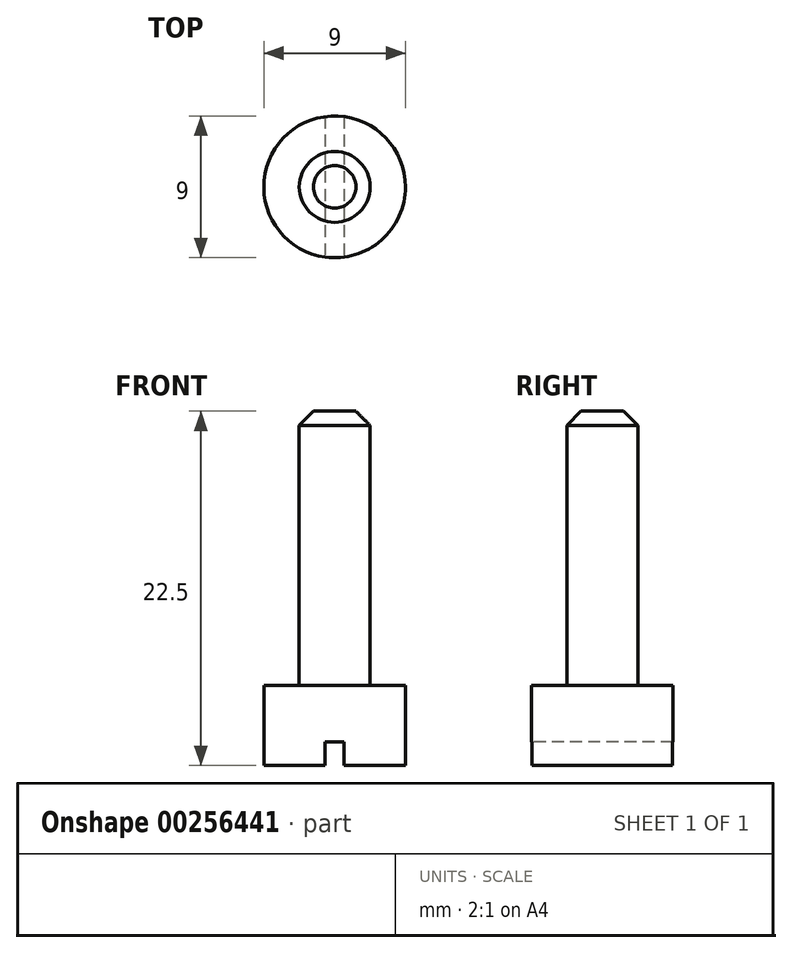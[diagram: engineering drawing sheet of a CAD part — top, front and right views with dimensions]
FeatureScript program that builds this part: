
annotation { "Feature Type Name" : "Feature", "Feature Type Description" : "" }
export const myFeature = defineFeature(function(context is Context, id is Id, definition is map)
    precondition{}
    {
        {
            var Q0;
            Q0=qCreatedBy(makeId("Top.planeOp"),FACE);
            var sketch = newSketch(context, id + "F0", { "sketchPlane" : qUnion([Q0])});
            skArc(sketch, "E0", {"start": v(-0.2, 1.49) * mm, "mid": v(-1.5, 0) * mm, "end": v(-0.2, -1.49) * mm});
            skLineSegment(sketch, "E1", {"start": v(-0.2, 1.49) * mm, "end": v(-0.2, -1.49) * mm});
            skLineSegment(sketch, "E2", {"start": v(0.2, 1.49) * mm, "end": v(0.2, -1.49) * mm});
            skArc(sketch, "E3.trimOffspring", {"start": v(0.2, -1.49) * mm, "mid": v(1.5, 0) * mm, "end": v(0.2, 1.49) * mm});
            skSolve(sketch);
        }
        {
            var Q0;
            {Q0=qUnion([makeQuery(id+"F0.imprint","IMPRINT",FACE,{"disambiguationData":[TD([[makeQuery(id+"F0.imprint","IMPRINT",EDGE,{"derivedFrom":sQuery(id+"F0.wireOp",EDGE,"E0")}),1.0]])]}),makeQuery(id+"F0.imprint","IMPRINT",FACE,{"disambiguationData":[TD([[makeQuery(id+"F0.imprint","IMPRINT",EDGE,{"derivedFrom":sQuery(id+"F0.wireOp",EDGE,"E2")}),1.0]])]})]);}
            extrude(context, id + "F1", {"entities" : qUnion([Q0]), "depth" : 0.5 * mm});
        }
        {
            var Q0;
            Q0=makeQuery(id+"F1.opExtrude","CAP_FACE",FACE,{"disambiguationData":[OSD([sQuery(id+"F0.wireOp",EDGE,"E0"),sQuery(id+"F0.wireOp",EDGE,"E1")])],"isStart":false});
            var sketch = newSketch(context, id + "F2", { "sketchPlane" : qUnion([Q0])});
            skCircle(sketch, "E4", {"center": v(0, 0) * mm, "radius": 1.5 * mm});
            skSolve(sketch);
        }
        {
            var Q0;
            {var subQ0=makeQuery(id+"F1.opExtrude","CAP_EDGE",EDGE,{"disambiguationData":[OSD([sQuery(id+"F0.wireOp",EDGE,"E1")])],"isStart":false});Q0=makeQuery(id+"F2.imprint","IMPRINT",FACE,{"disambiguationData":[TD([[makeQuery(id+"F2.imprint","IMPRINT",EDGE,{"derivedFrom":subQ0}),-1.0]])]});}
            var Q1;
            {var subQ0=makeQuery(id+"F1.opExtrude","CAP_EDGE",EDGE,{"disambiguationData":[OSD([sQuery(id+"F0.wireOp",EDGE,"E1")])],"isStart":false});Q1=makeQuery(id+"F2.imprint","IMPRINT",FACE,{"disambiguationData":[TD([[makeQuery(id+"F2.imprint","IMPRINT",EDGE,{"derivedFrom":subQ0}),1.0]])]});}
            extrude(context, id + "F3", {"entities" : qUnion([Q0, Q1]), "operationType" : NewBodyOperationType.ADD, "depth" : 1.2 * mm});
        }
        {
            var Q0;
            Q0=makeQuery(id+"F3.opExtrude","CAP_FACE",FACE,{"disambiguationData":[OSD([sQuery(id+"F2.wireOp",EDGE,"E4")])],"isStart":false});
            var sketch = newSketch(context, id + "F4", { "sketchPlane" : qUnion([Q0])});
            skCircle(sketch, "E5", {"center": v(0, 0) * mm, "radius": 0.75 * mm});
            skSolve(sketch);
        }
        {
            var Q0;
            Q0=makeQuery(id+"F4.imprint","IMPRINT",FACE,{"disambiguationData":[TD([[makeQuery(id+"F4.imprint","IMPRINT",EDGE,{"derivedFrom":sQuery(id+"F4.wireOp",EDGE,"E5")}),1.0]])]});
            extrude(context, id + "F5", {"entities" : qUnion([Q0]), "operationType" : NewBodyOperationType.ADD, "depth" : 2 * mm});
        }
        {
            var Q0;
            Q0=makeQuery(id+"F5.opExtrude","CAP_FACE",FACE,{"disambiguationData":[OSD([sQuery(id+"F4.wireOp",EDGE,"E5")])],"isStart":false});
            var sketch = newSketch(context, id + "F6", { "sketchPlane" : qUnion([Q0])});
            skCircle(sketch, "E6", {"center": v(0, 0) * mm, "radius": 0.75 * mm});
            skSolve(sketch);
        }
        {
            var Q0;
            Q0=makeQuery(id+"F6.imprint","IMPRINT",FACE,{"disambiguationData":[TD([[makeQuery(id+"F6.imprint","IMPRINT",EDGE,{"derivedFrom":sQuery(id+"F6.wireOp",EDGE,"E6")}),1.0]])]});
            extrude(context, id + "F7", {"entities" : qUnion([Q0]), "operationType" : NewBodyOperationType.ADD, "depth" : 3.8 * mm});
        }
        {
            var Q0;
            Q0=makeQuery(id+"F7.opExtrude","CAP_EDGE",EDGE,{"disambiguationData":[OSD([sQuery(id+"F6.wireOp",EDGE,"E6")])],"isStart":false});
            chamfer(context, id + "F8", {"entities" : qUnion([Q0]), "width" : 0.3 * mm, "tangentPropagation" : true});
        }
        {
            var Q0;
            Q0=makeQuery(id+"F1.opExtrude","SWEPT_BODY",BODY,{"disambiguationData":[OSD([sQuery(id+"F0.wireOp",EDGE,"E0"),sQuery(id+"F0.wireOp",EDGE,"E1")])]});
            var Q1;
            Q1=qCreatedBy(makeId("Origin.pointOp"),VERTEX);
            transform(context, id + "F9", {"entities" : qUnion([Q0]), "transformType" : TransformType.SCALE_UNIFORMLY, "scale" : 3, "makeCopy" : false, "scalePoint" : qUnion([Q1])});
        }
    });
